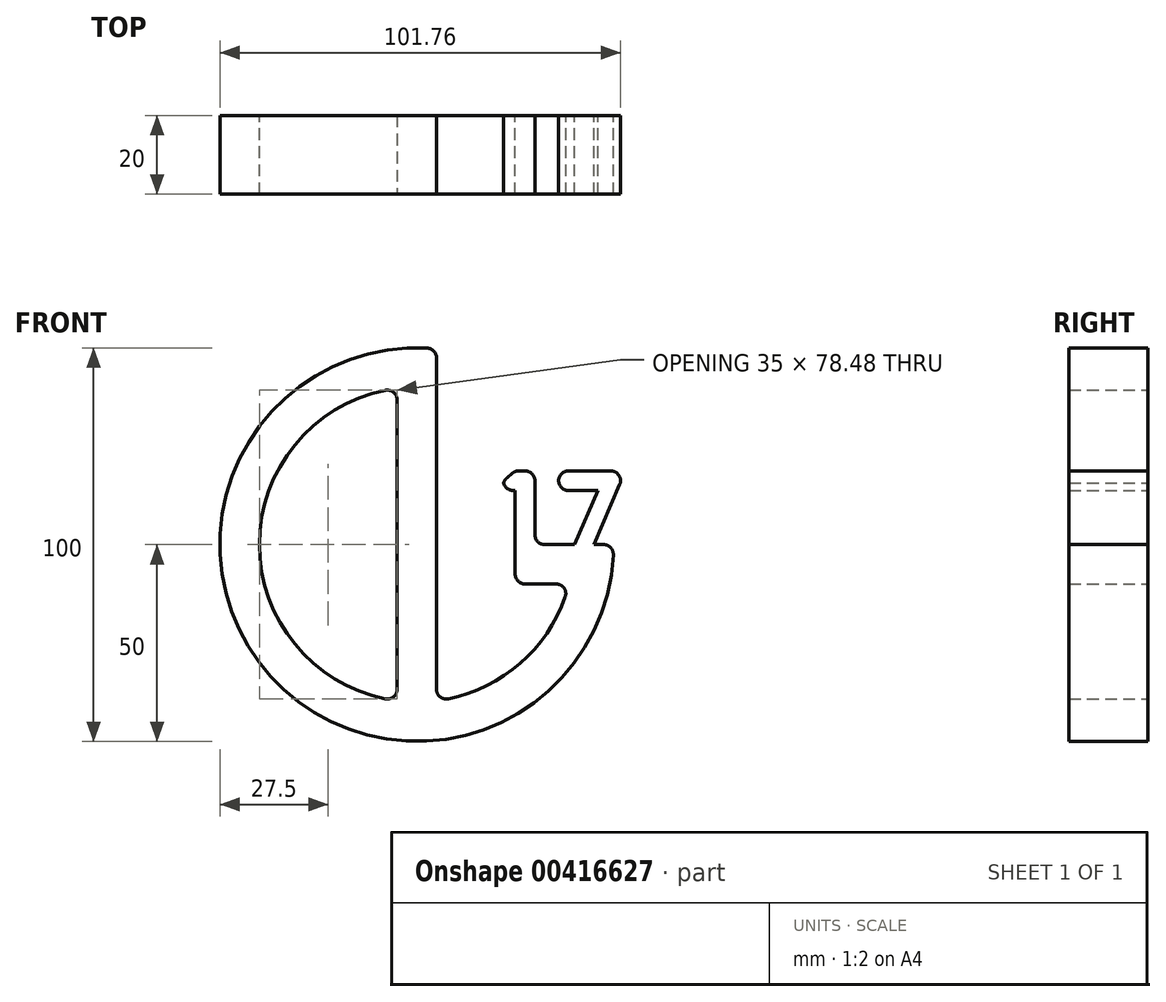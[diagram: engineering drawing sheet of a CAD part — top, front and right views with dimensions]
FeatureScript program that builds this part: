
annotation { "Feature Type Name" : "Feature", "Feature Type Description" : "" }
export const myFeature = defineFeature(function(context is Context, id is Id, definition is map)
    precondition{}
    {
        {
            var Q0;
            Q0=qCreatedBy(makeId("Front.planeOp"),FACE);
            var sketch = newSketch(context, id + "F0", { "sketchPlane" : qUnion([Q0])});
            skLineSegment(sketch, "E0", {"start": v(-5, 0) * mm, "end": v(-5, 39.69) * mm});
            skLineSegment(sketch, "E1", {"start": v(-5, 0) * mm, "end": v(-5, -39.69) * mm});
            skLineSegment(sketch, "E2", {"start": v(5, 0) * mm, "end": v(5, -39.69) * mm});
            skLineSegment(sketch, "E3", {"start": v(5, 0) * mm, "end": v(5, 49.75) * mm});
            skLineSegment(sketch, "E4", {"start": v(25, 0) * mm, "end": v(25, -10) * mm});
            skLineSegment(sketch, "E5", {"start": v(25, -10) * mm, "end": v(38.73, -10) * mm});
            skArc(sketch, "E6", {"start": v(-5, 39.69) * mm, "mid": v(-40, 0) * mm, "end": v(-5, -39.69) * mm});
            skArc(sketch, "E7", {"start": v(5, -39.69) * mm, "mid": v(26.43, -30.03) * mm, "end": v(38.73, -10) * mm});
            skArc(sketch, "E8", {"start": v(5, 49.75) * mm, "mid": v(-37.08, -33.54) * mm, "end": v(50, 0) * mm});
            skLineSegment(sketch, "E9", {"start": v(40, 0) * mm, "end": v(46.05, 13.73) * mm});
            skLineSegment(sketch, "E10", {"start": v(46.05, 13.73) * mm, "end": v(36.05, 13.73) * mm});
            skLineSegment(sketch, "E11", {"start": v(36.05, 13.73) * mm, "end": v(36.05, 18.73) * mm});
            skLineSegment(sketch, "E12", {"start": v(36.05, 18.73) * mm, "end": v(53.05, 18.73) * mm});
            skLineSegment(sketch, "E13", {"start": v(45, 0) * mm, "end": v(53.05, 18.73) * mm});
            skLineSegment(sketch, "E14", {"start": v(25, 0) * mm, "end": v(25, 13.73) * mm});
            skLineSegment(sketch, "E15", {"start": v(25, 13.73) * mm, "end": v(22, 13.73) * mm});
            skLineSegment(sketch, "E16", {"start": v(22, 13.73) * mm, "end": v(22, 16.23) * mm});
            skLineSegment(sketch, "E17", {"start": v(22, 16.23) * mm, "end": v(25, 18.73) * mm});
            skPoint(sketch, "E17.endSnap0", {"position": v(23.43, 18.73) * mm});
            skLineSegment(sketch, "E18", {"start": v(25, 18.73) * mm, "end": v(30, 18.73) * mm});
            skLineSegment(sketch, "E19", {"start": v(30, 18.73) * mm, "end": v(30, 0) * mm});
            skLineSegment(sketch, "E20", {"start": v(30, 0) * mm, "end": v(40, 0) * mm});
            skLineSegment(sketch, "E21", {"start": v(45, 0) * mm, "end": v(50, 0) * mm});
            skSolve(sketch);
        }
        {
            var Q0;
            Q0=makeQuery(id+"F0.imprint","IMPRINT",FACE,{"disambiguationData":[TD([[makeQuery(id+"F0.imprint","IMPRINT",EDGE,{"derivedFrom":sQuery(id+"F0.wireOp",EDGE,"E0")}),-1.0]])]});
            extrude(context, id + "F1", {"entities" : qUnion([Q0]), "depth" : 20 * mm});
        }
        {
            var Q0;
            Q0=makeQuery(id+"F1.opExtrude","SWEPT_EDGE",EDGE,{"disambiguationData":[OSD([sQuery(id+"F0.wireOp",EDGE,"E3"),sQuery(id+"F0.wireOp",EDGE,"E8")])]});
            var Q1;
            Q1=makeQuery(id+"F1.opExtrude","SWEPT_EDGE",EDGE,{"disambiguationData":[OSD([sQuery(id+"F0.wireOp",EDGE,"E12"),sQuery(id+"F0.wireOp",EDGE,"E13")])]});
            var Q2;
            Q2=makeQuery(id+"F1.opExtrude","SWEPT_EDGE",EDGE,{"disambiguationData":[OSD([sQuery(id+"F0.wireOp",EDGE,"E18"),sQuery(id+"F0.wireOp",EDGE,"E19")])]});
            var Q3;
            Q3=makeQuery(id+"F1.opExtrude","SWEPT_EDGE",EDGE,{"disambiguationData":[OSD([sQuery(id+"F0.wireOp",EDGE,"E8"),sQuery(id+"F0.wireOp",EDGE,"E21")])]});
            var Q4;
            Q4=makeQuery(id+"F1.opExtrude","SWEPT_EDGE",EDGE,{"disambiguationData":[OSD([sQuery(id+"F0.wireOp",EDGE,"E19"),sQuery(id+"F0.wireOp",EDGE,"E20")])]});
            var Q5;
            Q5=makeQuery(id+"F1.opExtrude","SWEPT_EDGE",EDGE,{"disambiguationData":[OSD([sQuery(id+"F0.wireOp",EDGE,"E17"),sQuery(id+"F0.wireOp",EDGE,"E18")])]});
            var Q6;
            Q6=makeQuery(id+"F1.opExtrude","SWEPT_EDGE",EDGE,{"disambiguationData":[OSD([sQuery(id+"F0.wireOp",EDGE,"E16"),sQuery(id+"F0.wireOp",EDGE,"E17")])]});
            var Q7;
            Q7=makeQuery(id+"F1.opExtrude","SWEPT_EDGE",EDGE,{"disambiguationData":[OSD([sQuery(id+"F0.wireOp",EDGE,"E15"),sQuery(id+"F0.wireOp",EDGE,"E16")])]});
            var Q8;
            Q8=makeQuery(id+"F1.opExtrude","SWEPT_EDGE",EDGE,{"disambiguationData":[OSD([sQuery(id+"F0.wireOp",EDGE,"E4"),sQuery(id+"F0.wireOp",EDGE,"E5")])]});
            var Q9;
            Q9=makeQuery(id+"F1.opExtrude","SWEPT_EDGE",EDGE,{"disambiguationData":[OSD([sQuery(id+"F0.wireOp",EDGE,"E5"),sQuery(id+"F0.wireOp",EDGE,"E7")])]});
            var Q10;
            Q10=makeQuery(id+"F1.opExtrude","SWEPT_EDGE",EDGE,{"disambiguationData":[OSD([sQuery(id+"F0.wireOp",EDGE,"E0"),sQuery(id+"F0.wireOp",EDGE,"E6")])]});
            var Q11;
            Q11=makeQuery(id+"F1.opExtrude","SWEPT_EDGE",EDGE,{"disambiguationData":[OSD([sQuery(id+"F0.wireOp",EDGE,"E1"),sQuery(id+"F0.wireOp",EDGE,"E6")])]});
            var Q12;
            Q12=makeQuery(id+"F1.opExtrude","SWEPT_EDGE",EDGE,{"disambiguationData":[OSD([sQuery(id+"F0.wireOp",EDGE,"E2"),sQuery(id+"F0.wireOp",EDGE,"E7")])]});
            var Q13;
            Q13=makeQuery(id+"F1.opExtrude","SWEPT_EDGE",EDGE,{"disambiguationData":[OSD([sQuery(id+"F0.wireOp",EDGE,"E11"),sQuery(id+"F0.wireOp",EDGE,"E12")])]});
            var Q14;
            Q14=makeQuery(id+"F1.opExtrude","SWEPT_EDGE",EDGE,{"disambiguationData":[OSD([sQuery(id+"F0.wireOp",EDGE,"E10"),sQuery(id+"F0.wireOp",EDGE,"E11")])]});
            fillet(context, id + "F2", {"entities" : qUnion([Q0, Q1, Q2, Q3, Q4, Q5, Q6, Q7, Q8, Q9, Q10, Q11, Q12, Q13, Q14]), "radius" : 2.5 * mm, "tangentPropagation" : true, "allowEdgeOverflow" : false});
        }
    });
